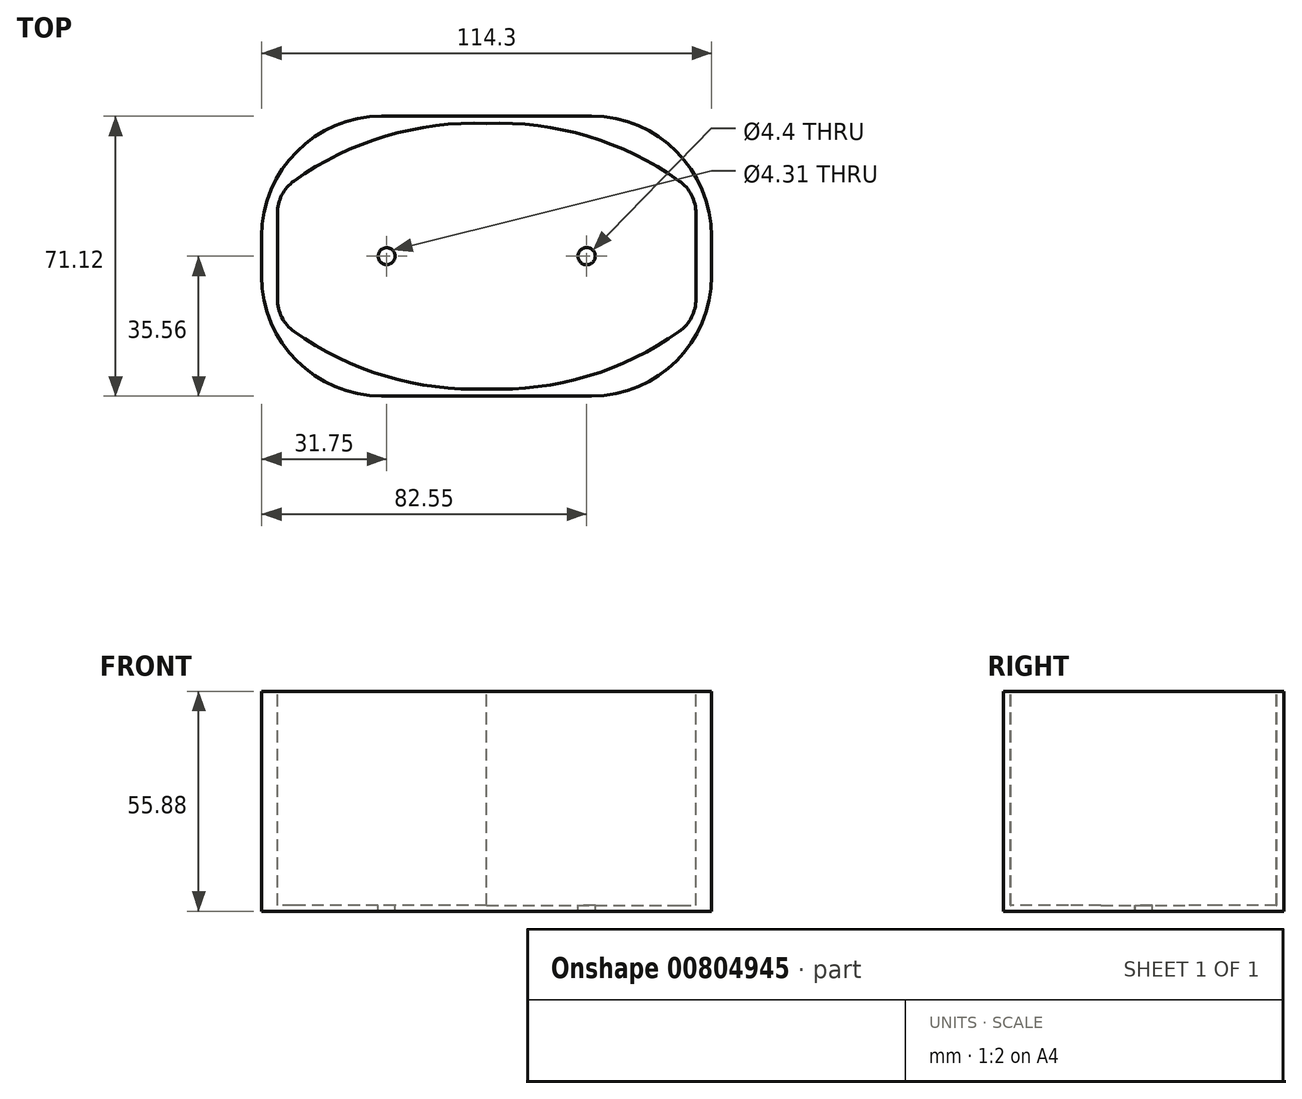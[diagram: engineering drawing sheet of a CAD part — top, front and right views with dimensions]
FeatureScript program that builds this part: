
annotation { "Feature Type Name" : "Feature", "Feature Type Description" : "" }
export const myFeature = defineFeature(function(context is Context, id is Id, definition is map)
    precondition{}
    {
        {
            var Q0;
            Q0=qCreatedBy(makeId("Top.planeOp"),FACE);
            var sketch = newSketch(context, id + "F0", { "sketchPlane" : qUnion([Q0])});
            skLineSegment(sketch, "E0.bottom", {"start": v(-26.67, 35.56) * mm, "end": v(26.67, 35.56) * mm});
            skLineSegment(sketch, "E0.top", {"start": v(-26.67, -35.56) * mm, "end": v(26.67, -35.56) * mm});
            skLineSegment(sketch, "E0.left", {"start": v(-57.15, 5.08) * mm, "end": v(-57.15, -5.08) * mm});
            skLineSegment(sketch, "E0.right", {"start": v(57.15, 5.08) * mm, "end": v(57.15, -5.08) * mm});
            skPoint(sketch, "E0.middle", {"position": v(0, 0) * mm});
            skPoint(sketch, "E1.visualSharp", {"position": v(-57.15, 35.56) * mm});
            skArc(sketch, "E1.filletArc", {"start": v(-26.67, 35.56) * mm, "mid": v(-48.22, 26.63) * mm, "end": v(-57.15, 5.08) * mm});
            skPoint(sketch, "E2.visualSharp", {"position": v(-57.15, -35.56) * mm});
            skArc(sketch, "E2.filletArc", {"start": v(-57.15, -5.08) * mm, "mid": v(-48.22, -26.63) * mm, "end": v(-26.67, -35.56) * mm});
            skPoint(sketch, "E3.visualSharp", {"position": v(57.15, -35.56) * mm});
            skArc(sketch, "E3.filletArc", {"start": v(26.67, -35.56) * mm, "mid": v(48.22, -26.63) * mm, "end": v(57.15, -5.08) * mm});
            skPoint(sketch, "E4.visualSharp", {"position": v(57.15, 35.56) * mm});
            skArc(sketch, "E4.filletArc", {"start": v(57.15, 5.08) * mm, "mid": v(48.22, 26.63) * mm, "end": v(26.67, 35.56) * mm});
            skSolve(sketch);
        }
        {
            var Q0;
            Q0=qSketchRegion(id+"F0",true);
            extrude(context, id + "F1", {"entities" : qUnion([Q0]), "depth" : 55.88 * mm, "offsetDistance" : 25.4 * mm});
        }
        {
            var Q0;
            Q0=makeQuery(id+"F1.opExtrude","CAP_FACE",FACE,{"disambiguationData":[OSD([sQuery(id+"F0.wireOp",EDGE,"E0.bottom"),sQuery(id+"F0.wireOp",EDGE,"E0.top"),sQuery(id+"F0.wireOp",EDGE,"E0.left"),sQuery(id+"F0.wireOp",EDGE,"E0.right"),sQuery(id+"F0.wireOp",EDGE,"E1.filletArc"),sQuery(id+"F0.wireOp",EDGE,"E2.filletArc"),sQuery(id+"F0.wireOp",EDGE,"E3.filletArc"),sQuery(id+"F0.wireOp",EDGE,"E4.filletArc")])],"isStart":false});
            var sketch = newSketch(context, id + "F2", { "sketchPlane" : qUnion([Q0])});
            skArc(sketch, "E5", {"start": v(0, 33.73) * mm, "mid": v(-25.67, 30.5) * mm, "end": v(-48.91, 19.14) * mm});
            skPoint(sketch, "E6.visualSharp", {"position": v(-51.39, 17.3) * mm});
            skLineSegment(sketch, "E7", {"start": v(-53.18, 10.86) * mm, "end": v(-53.18, 0) * mm});
            skPoint(sketch, "E8.visualSharp", {"position": v(-53.18, 15.87) * mm});
            skArc(sketch, "E8.filletArc", {"start": v(-48.91, 19.14) * mm, "mid": v(-52.05, 15.52) * mm, "end": v(-53.18, 10.86) * mm});
            skLineSegment(sketch, "E9.MirrorCS", {"start": v(-53.18, -10.86) * mm, "end": v(-53.18, 0) * mm});
            skArc(sketch, "E10.MirrorCS", {"start": v(-48.91, -19.14) * mm, "mid": v(-52.05, -15.52) * mm, "end": v(-53.18, -10.86) * mm});
            skArc(sketch, "E11.MirrorCS", {"start": v(0, -33.73) * mm, "mid": v(-25.67, -30.5) * mm, "end": v(-48.91, -19.14) * mm});
            skArc(sketch, "E12.MirrorCS", {"start": v(0, 33.73) * mm, "mid": v(25.67, 30.5) * mm, "end": v(48.91, 19.14) * mm});
            skArc(sketch, "E13.MirrorCS", {"start": v(48.91, 19.14) * mm, "mid": v(52.05, 15.52) * mm, "end": v(53.18, 10.86) * mm});
            skLineSegment(sketch, "E14.MirrorCS", {"start": v(53.18, 10.86) * mm, "end": v(53.18, 0) * mm});
            skLineSegment(sketch, "E15.MirrorCS", {"start": v(53.18, -10.86) * mm, "end": v(53.18, 0) * mm});
            skArc(sketch, "E16.MirrorCS", {"start": v(48.91, -19.14) * mm, "mid": v(52.05, -15.52) * mm, "end": v(53.18, -10.86) * mm});
            skArc(sketch, "E17.MirrorCS", {"start": v(0, -33.73) * mm, "mid": v(25.67, -30.5) * mm, "end": v(48.91, -19.14) * mm});
            skSolve(sketch);
        }
        {
            var Q0;
            Q0=qSketchRegion(id+"F2",true);
            var Q1;
            Q1=makeQuery(id+"F1.opExtrude","CAP_FACE",FACE,{"disambiguationData":[OSD([sQuery(id+"F0.wireOp",EDGE,"E0.bottom"),sQuery(id+"F0.wireOp",EDGE,"E0.top"),sQuery(id+"F0.wireOp",EDGE,"E0.left"),sQuery(id+"F0.wireOp",EDGE,"E0.right"),sQuery(id+"F0.wireOp",EDGE,"E1.filletArc"),sQuery(id+"F0.wireOp",EDGE,"E2.filletArc"),sQuery(id+"F0.wireOp",EDGE,"E3.filletArc"),sQuery(id+"F0.wireOp",EDGE,"E4.filletArc")])],"isStart":true});
            extrude(context, id + "F3", {"entities" : qUnion([Q0]), "operationType" : NewBodyOperationType.REMOVE, "endBound" : BoundingType.UP_TO_SURFACE, "oppositeDirection" : true, "depth" : 25.4 * mm, "endBoundEntityFace" : qUnion([Q1]), "hasOffset" : true, "offsetDistance" : 1.5 * mm});
        }
        {
            var Q0;
            Q0=makeQuery(id+"F3.boolean.opBoolean","COPY",FACE,{"derivedFrom":makeQuery(id+"F3.opExtrude","CAP_FACE",FACE,{"disambiguationData":[OSD([sQuery(id+"F2.wireOp",EDGE,"E5"),sQuery(id+"F2.wireOp",EDGE,"E7"),sQuery(id+"F2.wireOp",EDGE,"E8.filletArc"),sQuery(id+"F2.wireOp",EDGE,"E9.MirrorCS"),sQuery(id+"F2.wireOp",EDGE,"E10.MirrorCS"),sQuery(id+"F2.wireOp",EDGE,"E11.MirrorCS"),sQuery(id+"F2.wireOp",EDGE,"E12.MirrorCS"),sQuery(id+"F2.wireOp",EDGE,"E13.MirrorCS"),sQuery(id+"F2.wireOp",EDGE,"E14.MirrorCS"),sQuery(id+"F2.wireOp",EDGE,"E15.MirrorCS"),sQuery(id+"F2.wireOp",EDGE,"E16.MirrorCS"),sQuery(id+"F2.wireOp",EDGE,"E17.MirrorCS")])],"isStart":false})});
            var sketch = newSketch(context, id + "F4", { "sketchPlane" : qUnion([Q0])});
            skCircle(sketch, "E18", {"center": v(-25.4, 0) * mm, "radius": 2.16 * mm});
            skCircle(sketch, "E19", {"center": v(25.4, 0) * mm, "radius": 2.2 * mm});
            skSolve(sketch);
        }
        {
            var Q0;
            Q0=qSketchRegion(id+"F4",true);
            extrude(context, id + "F5", {"entities" : qUnion([Q0]), "operationType" : NewBodyOperationType.REMOVE, "endBound" : BoundingType.THROUGH_ALL, "oppositeDirection" : true, "depth" : 25.4 * mm, "offsetDistance" : 25.4 * mm});
        }
    });
